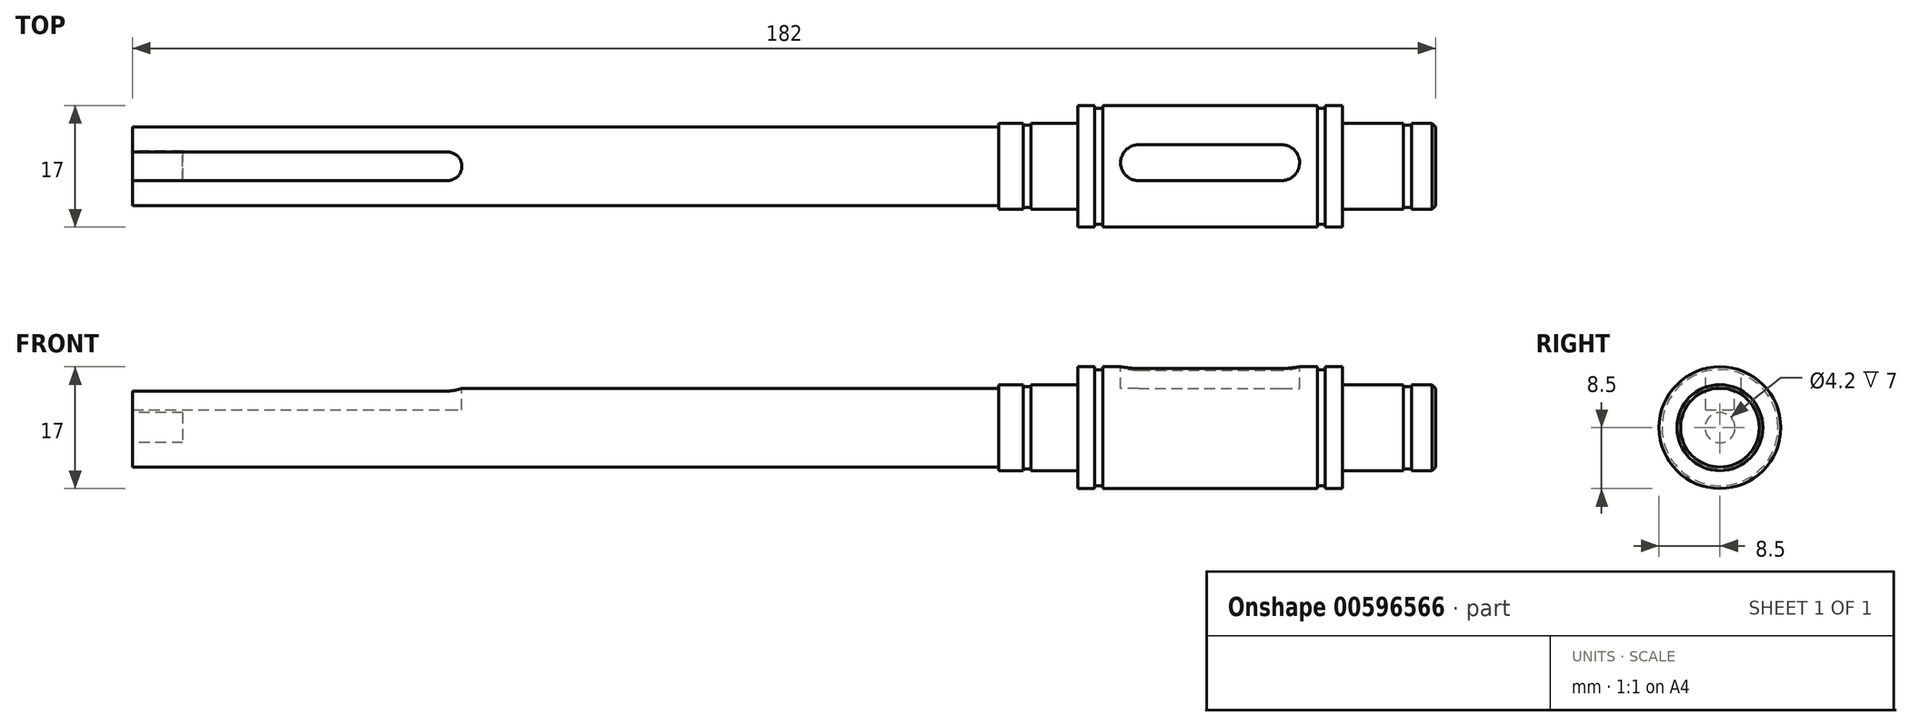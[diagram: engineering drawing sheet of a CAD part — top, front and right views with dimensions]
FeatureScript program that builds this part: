
annotation { "Feature Type Name" : "Feature", "Feature Type Description" : "" }
export const myFeature = defineFeature(function(context is Context, id is Id, definition is map)
    precondition{}
    {
        {
            var Q0;
            Q0=qCreatedBy(makeId("Front.planeOp"),FACE);
            var sketch = newSketch(context, id + "F0", { "sketchPlane" : qUnion([Q0])});
            skLineSegment(sketch, "E0", {"start": v(0, 0) * mm, "end": v(182, 0) * mm});
            skLineSegment(sketch, "E1", {"start": v(0, 0) * mm, "end": v(0, 5.5) * mm});
            skLineSegment(sketch, "E2", {"start": v(0, 5.5) * mm, "end": v(121, 5.5) * mm});
            skLineSegment(sketch, "E3", {"start": v(121, 5.5) * mm, "end": v(121, 6) * mm});
            skLineSegment(sketch, "E4", {"start": v(121, 6) * mm, "end": v(124.4, 6) * mm});
            skLineSegment(sketch, "E5", {"start": v(132, 6) * mm, "end": v(132, 8.5) * mm});
            skLineSegment(sketch, "E6", {"start": v(132, 8.5) * mm, "end": v(134.4, 8.5) * mm});
            skLineSegment(sketch, "E7", {"start": v(169, 8.5) * mm, "end": v(169, 6) * mm});
            skLineSegment(sketch, "E8", {"start": v(169, 6) * mm, "end": v(177.5, 6) * mm});
            skLineSegment(sketch, "E9", {"start": v(182, 6) * mm, "end": v(182, 0) * mm});
            skLineSegment(sketch, "E10.0", {"start": v(178.6, 6) * mm, "end": v(178.6, 5.75) * mm});
            skLineSegment(sketch, "E11.0", {"start": v(177.5, 6) * mm, "end": v(177.5, 5.75) * mm});
            skLineSegment(sketch, "E12.0", {"start": v(177.5, 5.75) * mm, "end": v(178.6, 5.75) * mm});
            skLineSegment(sketch, "E13.trimOffspring", {"start": v(178.6, 6) * mm, "end": v(182, 6) * mm});
            skLineSegment(sketch, "E14.0", {"start": v(166.6, 8.5) * mm, "end": v(166.6, 8.1) * mm});
            skLineSegment(sketch, "E15.0", {"start": v(165.5, 8.1) * mm, "end": v(166.6, 8.1) * mm});
            skLineSegment(sketch, "E16.0", {"start": v(165.5, 8.5) * mm, "end": v(165.5, 8.1) * mm});
            skLineSegment(sketch, "E17.trimOffspring", {"start": v(166.6, 8.5) * mm, "end": v(169, 8.5) * mm});
            skLineSegment(sketch, "E18.0", {"start": v(134.4, 8.1) * mm, "end": v(134.4, 8.5) * mm});
            skLineSegment(sketch, "E19.0", {"start": v(135.5, 8.1) * mm, "end": v(135.5, 8.5) * mm});
            skLineSegment(sketch, "E20.0", {"start": v(134.4, 8.1) * mm, "end": v(135.5, 8.1) * mm});
            skLineSegment(sketch, "E21.trimOffspring", {"start": v(135.5, 8.5) * mm, "end": v(165.5, 8.5) * mm});
            skLineSegment(sketch, "E22.0", {"start": v(124.4, 5.75) * mm, "end": v(124.4, 6) * mm});
            skLineSegment(sketch, "E23.0", {"start": v(125.5, 5.75) * mm, "end": v(125.5, 6) * mm});
            skLineSegment(sketch, "E24.0", {"start": v(124.4, 5.75) * mm, "end": v(125.5, 5.75) * mm});
            skLineSegment(sketch, "E25.trimOffspring", {"start": v(125.5, 6) * mm, "end": v(132, 6) * mm});
            skSolve(sketch);
        }
        {
            var Q0;
            Q0 = qSketchRegion(id + "F0", true);
            var Q1;
            Q1=sQuery(id+"F0.wireOp",EDGE,"E0");
            revolve(context, id + "F1", {"surfaceOperationType" : NewSurfaceOperationType.NEW, "entities" : qUnion([Q0]), "axis" : qUnion([Q1]), "revolveType" : RevolveType.FULL});
        }
        {
            var Q0;
            Q0=qCreatedBy(makeId("Top.planeOp"),FACE);
            cPlane(context, id + "F2", {"entities" : qUnion([Q0]), "cplaneType" : CPlaneType.OFFSET, "offset" : 5.5 * mm, "width" : 150 * mm, "height" : 150 * mm});
        }
        {
            var Q0;
            Q0=qCreatedBy(id+"F2.planeOp",FACE);
            var sketch = newSketch(context, id + "F3", { "sketchPlane" : qUnion([Q0])});
            skLineSegment(sketch, "E26.bottom", {"start": v(0, -2) * mm, "end": v(44, -2) * mm});
            skLineSegment(sketch, "E26.top", {"start": v(0, 2) * mm, "end": v(44, 2) * mm});
            skLineSegment(sketch, "E26.left", {"start": v(0, -2) * mm, "end": v(0, 2) * mm});
            skLineSegment(sketch, "E26.right", {"start": v(46, 0) * mm, "end": v(46, 0) * mm});
            skPoint(sketch, "E27.visualSharp", {"position": v(46, 2) * mm});
            skArc(sketch, "E27.filletArc", {"start": v(46, 0) * mm, "mid": v(45.41, 1.41) * mm, "end": v(44, 2) * mm});
            skPoint(sketch, "E28.visualSharp", {"position": v(46, -2) * mm});
            skArc(sketch, "E28.filletArc", {"start": v(44, -2) * mm, "mid": v(45.41, -1.41) * mm, "end": v(46, 0) * mm});
            skSolve(sketch);
        }
        {
            var Q0;
            Q0 = qSketchRegion(id + "F3", true);
            extrude(context, id + "F4", {"entities" : qUnion([Q0]), "operationType" : NewBodyOperationType.REMOVE, "oppositeDirection" : true, "depth" : 3 * mm, "offsetDistance" : 25 * mm});
        }
        {
            var Q0;
            Q0=qCreatedBy(makeId("Top.planeOp"),FACE);
            cPlane(context, id + "F5", {"entities" : qUnion([Q0]), "cplaneType" : CPlaneType.OFFSET, "offset" : (17 / 2) * mm, "width" : 150 * mm, "height" : 150 * mm});
        }
        {
            var Q0;
            Q0=qCreatedBy(id+"F5.planeOp",FACE);
            var sketch = newSketch(context, id + "F6", { "sketchPlane" : qUnion([Q0])});
            skLineSegment(sketch, "E29.bottom", {"start": v(140.5, -2) * mm, "end": v(160.5, -2) * mm});
            skLineSegment(sketch, "E29.top", {"start": v(140.5, 3) * mm, "end": v(160.5, 3) * mm});
            skLineSegment(sketch, "E29.left", {"start": v(138, 0.5) * mm, "end": v(138, 0.5) * mm});
            skLineSegment(sketch, "E29.right", {"start": v(163, 0.5) * mm, "end": v(163, 0.5) * mm});
            skPoint(sketch, "E30.visualSharp", {"position": v(138, 3) * mm});
            skArc(sketch, "E30.filletArc", {"start": v(140.5, 3) * mm, "mid": v(138.73, 2.27) * mm, "end": v(138, 0.5) * mm});
            skPoint(sketch, "E31.visualSharp", {"position": v(138, -2) * mm});
            skArc(sketch, "E31.filletArc", {"start": v(138, 0.5) * mm, "mid": v(138.73, -1.27) * mm, "end": v(140.5, -2) * mm});
            skPoint(sketch, "E32.visualSharp", {"position": v(163, 3) * mm});
            skArc(sketch, "E32.filletArc", {"start": v(163, 0.5) * mm, "mid": v(162.27, 2.27) * mm, "end": v(160.5, 3) * mm});
            skPoint(sketch, "E33.visualSharp", {"position": v(163, -2) * mm});
            skArc(sketch, "E33.filletArc", {"start": v(160.5, -2) * mm, "mid": v(162.27, -1.27) * mm, "end": v(163, 0.5) * mm});
            skSolve(sketch);
        }
        {
            var Q0;
            Q0=makeQuery(id+"F6.imprint","IMPRINT",FACE,{"disambiguationData":[TD([[makeQuery(id+"F6.imprint","IMPRINT",EDGE,{"derivedFrom":sQuery(id+"F6.wireOp",EDGE,"E29.bottom")}),1.0]])]});
            extrude(context, id + "F7", {"entities" : qUnion([Q0]), "operationType" : NewBodyOperationType.REMOVE, "oppositeDirection" : true, "depth" : 3 * mm, "offsetDistance" : 25 * mm});
        }
        {
            var Q0;
            Q0=makeQuery(id+"F1.opRevolve","SWEPT_FACE",FACE,{"disambiguationData":[OSD([sQuery(id+"F0.wireOp",EDGE,"E1")])]});
            var sketch = newSketch(context, id + "F8", { "sketchPlane" : qUnion([Q0])});
            skCircle(sketch, "E34", {"center": v(0, 0) * mm, "radius": 2.1 * mm});
            skSolve(sketch);
        }
        {
            var Q0;
            Q0=makeQuery(id+"F8.imprint","IMPRINT",FACE,{"disambiguationData":[TD([[makeQuery(id+"F8.imprint","IMPRINT",EDGE,{"derivedFrom":sQuery(id+"F8.wireOp",EDGE,"E34")}),1.0]])]});
            extrude(context, id + "F9", {"entities" : qUnion([Q0]), "operationType" : NewBodyOperationType.REMOVE, "oppositeDirection" : true, "depth" : 7 * mm, "offsetDistance" : 25 * mm});
        }
        {
            var Q0;
            Q0=makeQuery(id+"F1.opRevolve","SWEPT_EDGE",EDGE,{"disambiguationData":[OSD([sQuery(id+"F0.wireOp",EDGE,"E9"),sQuery(id+"F0.wireOp",EDGE,"E13.trimOffspring")])]});
            chamfer(context, id + "F10", {"entities" : qUnion([Q0]), "width" : .5 * mm, "tangentPropagation" : true});
        }
    });
